# Revit family: GQ Rosenberg 2
name_source: partatom
category: Wyposażenie mechaniczne
revit_build: Autodesk Revit 2017 (Build: 20160225_1515(x64)
units: mm (PartAtom-declared; Revit-internal decimal feet)

## family parameters
Oparty na płaszczyźnie roboczej = Nie
Punkt obliczania pomieszczeń = Nie
Tnij formami wycięć po wczytaniu = Nie
Typ części = Normalny
Współdzielony = Nie
Wymiar okrągłego złącza = Użyj średnicy
Zawsze pionowo = Tak

## types (6) — shared parameters
Częstotliwość = 50 Hz
Dlugosc_silnika_tyl = 50 mm  [stored 0.164042 ft]
Klasa szczelnosci silnika (IP) = IP54
Moc = 1 kW
Producent = Rosenberg
URL = https://www.rosenberg.pl

## per-type parameters (varying)
- 450 N.4FF KS: 450 N.4FF KS=Tak; 500 K.5FA KS=Nie; 500 N.4FF KS=Nie; 500 N.5HF KK=Nie; 560 N.5HF KK=Nie; Ciśnienie=129.0 Pa; Dlugosc_silnika_przod=50 mm  [stored 0.164042 ft]; Dlugosc_smigla=218 mm; Grubosc=86 mm  [stored 0.282152 ft]; Grubosc_plyty=14 mm  [stored 0.0459318 ft]; Maksymalna dopuszczalna temperatura przetłaczanego medium=45 °C; Masa=10.50 kg; Model=450 N.4FF KS; Napięcie=230 V; Obroty (1/min)=1390; Promien_wew=223 mm  [stored 0.731627 ft]; Promien_zew=245 mm  [stored 0.803806 ft]; Przepływ poowietrza=4425.0 m³/h; Prąd=2 A; S1=30 mm  [stored 0.0984252 ft]; Srednica_silnika=68 mm; Srednica_wew=446 mm  [stored 1.46325 ft]; Srednica_zewnetrzna=490 mm  [stored 1.60761 ft]; Wymiar_obudowy=575 mm; Wymiar_obudowy/2=288 mm
- 500 K.5FA KS: 450 N.4FF KS=Nie; 500 K.5FA KS=Tak; 500 N.4FF KS=Nie; 500 N.5HF KK=Nie; 560 N.5HF KK=Nie; Ciśnienie=219.0 Pa; Dlugosc_silnika_przod=50 mm  [stored 0.164042 ft]; Dlugosc_smigla=244 mm  [stored 0.800525 ft]; Grubosc=104 mm  [stored 0.341207 ft]; Grubosc_plyty=16 mm  [stored 0.0524934 ft]; Maksymalna dopuszczalna temperatura przetłaczanego medium=60 °C; Masa=15.00 kg; Model=500 K.5FA KS; Napięcie=230 V; Obroty (1/min)=1650; Promien_wew=249 mm  [stored 0.816929 ft]; Promien_zew=270 mm  [stored 0.885827 ft]; Przepływ poowietrza=6465.0 m³/h; Prąd=5 A; S1=0 mm  [stored 0 ft]; Srednica_silnika=80 mm  [stored 0.262467 ft]; Srednica_wew=497 mm; Srednica_zewnetrzna=540 mm  [stored 1.77165 ft]; Wymiar_obudowy=655 mm  [stored 2.14895 ft]; Wymiar_obudowy/2=328 mm
- 500 N.4FF KS: 450 N.4FF KS=Nie; 500 K.5FA KS=Nie; 500 N.4FF KS=Tak; 500 N.5HF KK=Nie; 560 N.5HF KK=Nie; Ciśnienie=109.0 Pa; Dlugosc_silnika_przod=50 mm  [stored 0.164042 ft]; Dlugosc_smigla=244 mm  [stored 0.800525 ft]; Grubosc=104 mm  [stored 0.341207 ft]; Grubosc_plyty=16 mm  [stored 0.0524934 ft]; Maksymalna dopuszczalna temperatura przetłaczanego medium=60 °C; Masa=13.50 kg; Model=500 N.4FF KS; Napięcie=230 V; Obroty (1/min)=1215; Promien_wew=249 mm  [stored 0.816929 ft]; Promien_zew=270 mm  [stored 0.885827 ft]; Przepływ poowietrza=5792.0 m³/h; Prąd=2 A; S1=0 mm  [stored 0 ft]; Srednica_silnika=75 mm; Srednica_wew=498 mm  [stored 1.63386 ft]; Srednica_zewnetrzna=539 mm  [stored 1.76837 ft]; Wymiar_obudowy=655 mm  [stored 2.14895 ft]; Wymiar_obudowy/2=328 mm
- 560 K.5HF KS: 450 N.4FF KS=Nie; 500 K.5FA KS=Nie; 500 N.4FF KS=Nie; 500 N.5HF KK=Nie; 560 N.5HF KK=Tak; Ciśnienie=162.0 Pa; Data=09.2018; Dlugosc_silnika_przod=50 mm  [stored 0.164042 ft]; Dlugosc_smigla=271 mm  [stored 0.889108 ft]; Grubosc=105 mm  [stored 0.344488 ft]; Grubosc_plyty=16 mm  [stored 0.0524934 ft]; Maksymalna dopuszczalna temperatura przetłaczanego medium=45 °C; Masa=23.00 kg; Model=560 K.5HF KS; Napięcie=230 V; Obroty (1/min)=1250; Promien_wew=276 mm  [stored 0.905512 ft]; Promien_zew=299 mm; Przepływ poowietrza=7874.0 m³/h; Prąd=4 A; S1=33 mm  [stored 0.108268 ft]; Srednica_silnika=70 mm  [stored 0.229659 ft]; Srednica_wew=552 mm  [stored 1.81102 ft]; Srednica_zewnetrzna=597 mm; Wersja=1; Wymiar_obudowy=725 mm  [stored 2.37861 ft]; Wymiar_obudowy/2=363 mm
- 500 N.5HF KK: 450 N.4FF KS=Nie; 500 K.5FA KS=Nie; 500 N.4FF KS=Nie; 500 N.5HF KK=Tak; 560 N.5HF KK=Nie; Ciśnienie=230.0 Pa; Dlugosc_silnika_przod=50 mm  [stored 0.164042 ft]; Dlugosc_smigla=271 mm  [stored 0.889108 ft]; Grubosc=120 mm  [stored 0.393701 ft]; Grubosc_plyty=15 mm  [stored 0.0492126 ft]; Maksymalna dopuszczalna temperatura przetłaczanego medium=60 °C; Masa=20.00 kg; Model=500 K.5HF KK; Napięcie=400 V; Obroty (1/min)=1650; Promien_wew=276 mm  [stored 0.905512 ft]; Promien_zew=299 mm; Przepływ poowietrza=6752.0 m³/h; Prąd=2 A; S1=0 mm  [stored 0 ft]; Srednica_silnika=70 mm  [stored 0.229659 ft]; Srednica_wew=552 mm  [stored 1.81102 ft]; Srednica_zewnetrzna=597 mm; Wymiar_obudowy=725 mm  [stored 2.37861 ft]; Wymiar_obudowy/2=363 mm
- 560 K.5HF KK: 450 N.4FF KS=Nie; 500 K.5FA KS=Nie; 500 N.4FF KS=Nie; 500 N.5HF KK=Nie; 560 N.5HF KK=Tak; Ciśnienie=197.0 Pa; Dlugosc_silnika_przod=55 mm  [stored 0.180446 ft]; Dlugosc_smigla=271 mm  [stored 0.889108 ft]; Grubosc=105 mm  [stored 0.344488 ft]; Grubosc_plyty=16 mm  [stored 0.0524934 ft]; Maksymalna dopuszczalna temperatura przetłaczanego medium=60 °C; Masa=22.50 kg; Model=560 K.5HF KS; Napięcie=440 V; Obroty (1/min)=1250; Promien_wew=276 mm  [stored 0.905512 ft]; Promien_zew=299 mm; Przepływ poowietrza=7671.0 m³/h; Prąd=2 A; S1=33 mm  [stored 0.108268 ft]; Srednica_silnika=70 mm  [stored 0.229659 ft]; Srednica_wew=552 mm  [stored 1.81102 ft]; Srednica_zewnetrzna=597 mm; Wymiar_obudowy=725 mm  [stored 2.37861 ft]; Wymiar_obudowy/2=363 mm

note: [stored X ft] marks values corroborated as IEEE doubles in the binary element streams (Revit-internal decimal feet)
